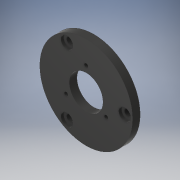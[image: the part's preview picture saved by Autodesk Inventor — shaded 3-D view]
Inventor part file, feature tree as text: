
AUTODESK INVENTOR PART (.ipt)
format: ipt  version: 2018 (Build 220112000, 112)  size: 285,696 bytes
history: native  units: in
note: dims shown in document units (in); Inventor stores cm internally (conversion verified against a paired STEP export)
features: sketch x3, extrude x2, hole x1, pattern_circular x1
ambient origin geometry x8: Origin, YZ Plane, XZ Plane, XY Plane, X Axis, Y Axis, Z Axis, Center Point
bodies: Solid1 (feature_tree)
feature tree (7):
  extrude  "Extrusion1"  Depth=2.3622in
  hole  "Hole1"  [1 undecoded]
  pattern_circular  "Circular Pattern2"  [2 undecoded]
  extrude  "Extrusion8"  Depth=0.3937in TaperAngle=0.0deg
  sketch  "Sketch1"  dims[d0=0.7874in d1=2.3622in]
  sketch  "Sketch4"  dims[d3=0.0984in d4=1.1811in d6=360.0deg]
  sketch  "Sketch5"  dims[d8=0.1969in d9=0.0in d34=0.0394in d35=0.3937in d36=0.0in d40=1.9685in d41=0.1772in d42=0.1772in d43=0.2362in d44=0.315in d45=0.0787in d46=90.0deg d47=0.315in d48=0.8108in d49=1.1811in d50=360.0deg]
note: 3 required parameter values undecoded (feature->parameter linkage not recoverable at this tier; creation-order binding heuristic only, values carry confidence <= 0.55)
